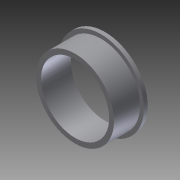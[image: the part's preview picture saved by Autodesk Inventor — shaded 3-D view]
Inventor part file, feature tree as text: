
AUTODESK INVENTOR PART (.ipt)
format: ipt  version: 2011 (Build 150239000, 239)  size: 93,184 bytes
history: native  units: in
note: dims shown in document units (in); Inventor stores cm internally (conversion verified against a paired STEP export)
features: extrude x3, sketch x3
ambient origin geometry x8: Origin, YZ Plane, XZ Plane, XY Plane, X Axis, Y Axis, Z Axis, Center Point
bodies: Solid1 (feature_tree)
feature tree (6):
  extrude  "Extrusion1"  Depth=0.03in TaperAngle=0.0deg
  extrude  "Extrusion2"  Depth=0.2in TaperAngle=0.0deg
  extrude  "Extrusion3"  TaperAngle=0.0deg  [1 undecoded]
  sketch  "Sketch1"  dims[d0=0.66in d2=0.03in d3=0.0in]
  sketch  "Sketch3"  dims[d13=0.6in d14=0.2in d15=0.0in]
  sketch  "Sketch4"  dims[d16=0.525in d17=0.0in d18=0.0in]
note: 1 required parameter value undecoded (feature->parameter linkage not recoverable at this tier; creation-order binding heuristic only, values carry confidence <= 0.55)
